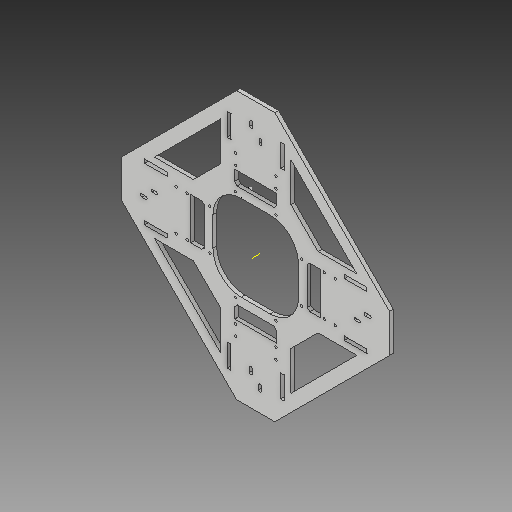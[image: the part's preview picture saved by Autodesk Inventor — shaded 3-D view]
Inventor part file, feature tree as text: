
AUTODESK INVENTOR PART (.ipt)
format: ipt  version: 2017 (Build 210142000, 142)  size: 366,080 bytes
history: native  units: in
note: dims shown in document units (in); Inventor stores cm internally (conversion verified against a paired STEP export)
features: reference x29, other x8, plane x2, extrude x1, chamfer x1, sketch x1
ambient origin geometry x8: Origin, YZ Plane, XZ Plane, XY Plane, X Axis, Y Axis, Z Axis, Center Point
bodies: Solid1 (feature_tree)
feature tree (42):
  extrude  "Extrusion1"  Depth=4.75in
  chamfer  "Chamfer1"  Distance=0.2087in
  other  "Work Axis1"
  sketch  "Sketch1"  dims[d0=4.75in d1=4.75in d7=0.2087in d8=0.0in d11=12.0in d12=12.0in d13=1.5748in d14=0.5906in d15=1.5748in d17=360.0deg d19=1.5in d20=0.125in d21=45.0deg d22=0.75in d24=1.25in d25=0.2087in d26=1.5748in d28=360.0deg d30=1.5748in d32=360.0deg d34=1.5748in d36=360.0deg]
  plane  "Work Plane1"
  plane  "Work Plane2"
  reference  "Reference4"
  reference  "Reference5"
  reference  "Reference6"
  reference  "Reference7"
  reference  "Reference9"
  reference  "Reference10"
  reference  "Reference11"
  reference  "Reference12"
  reference  "Reference13"
  reference  "Reference14"
  reference  "Reference15"
  reference  "Reference16"
  reference  "Reference17"
  reference  "Reference18"
  reference  "Reference19"
  reference  "Reference20"
  reference  "Reference21"
  reference  "Reference22"
  reference  "Reference23"
  reference  "Reference24"
  reference  "Reference25"
  reference  "Reference26"
  reference  "Reference27"
  reference  "Reference28"
  reference  "Reference29"
  reference  "Reference30"
  reference  "Reference31"
  reference  "Reference32"
  reference  "Reference33"
  other  "Rubiks Cube Solver.iam"
  other  "stepper mount:1"
  other  "bearing block:2"
  other  "riser:1"
  other  "bearing block:1"
  other  "leg:1"
  other  "leg:2"
